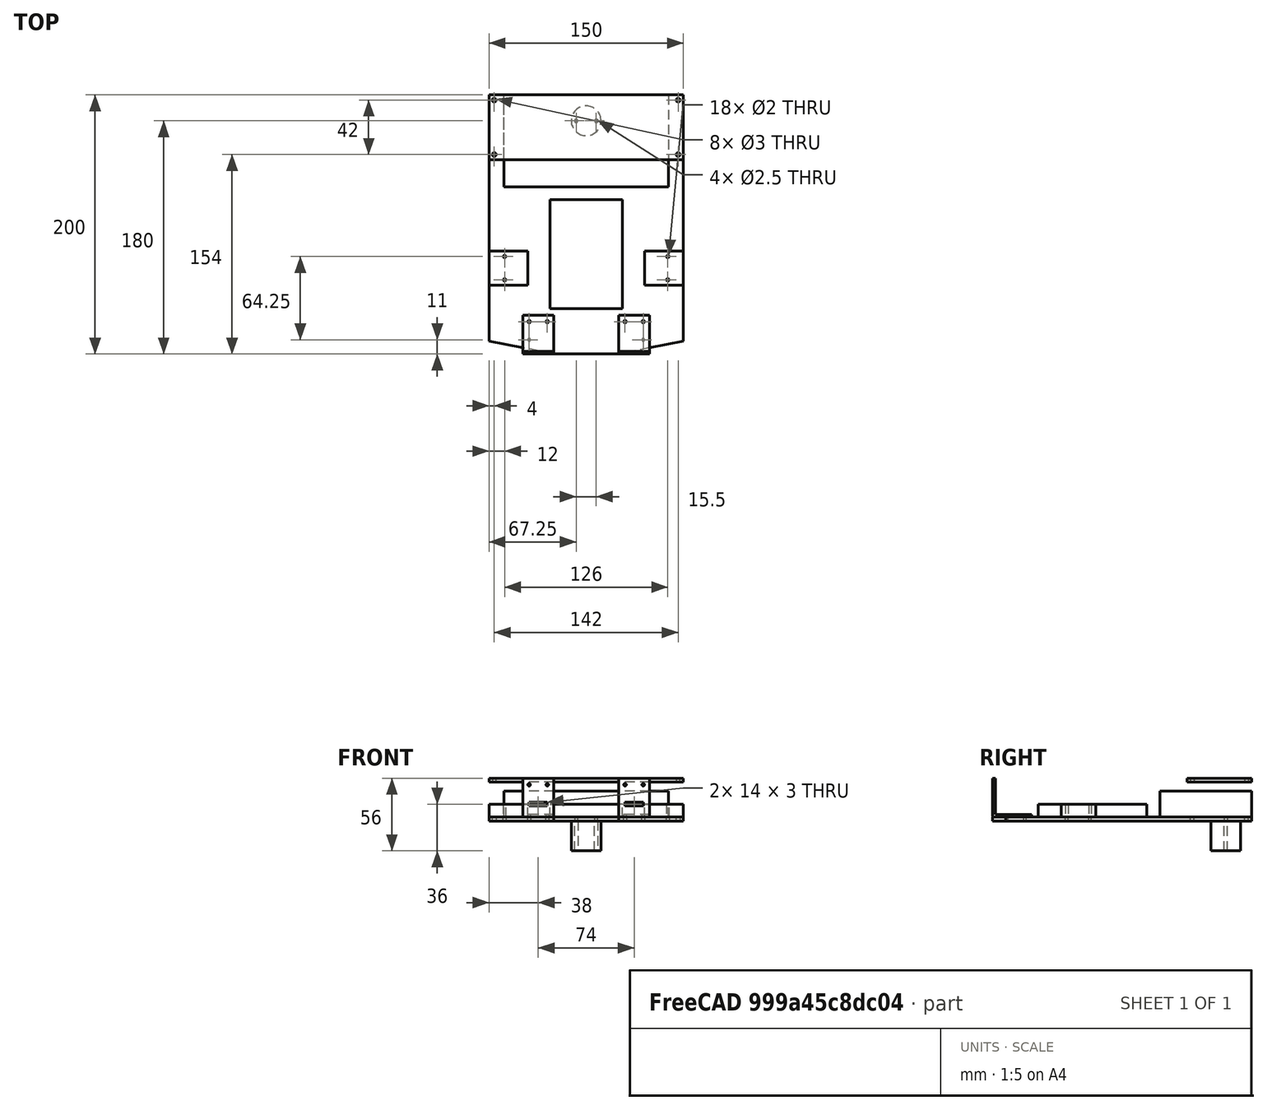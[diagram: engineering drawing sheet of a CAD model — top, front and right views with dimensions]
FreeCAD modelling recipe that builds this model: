
FCSTD DOCUMENT  (FreeCAD 0.21R30769 (Git))
Label: robot
License: All rights reserved
LicenseURL: http://en.wikipedia.org/wiki/All_rights_reserved
objects: TechDraw::DrawViewDimension×57, PartDesign::ShapeBinder×17, PartDesign::Pocket×12, PartDesign::Pad×11, PartDesign::Body×10, TechDraw::DrawProjGroupItem×10, Sketcher::SketchObject×8, TechDraw::DrawSVGTemplate×7, TechDraw::DrawProjGroup×7, TechDraw::DrawPage×7, PartDesign::SubShapeBinder×6, TechDraw::DrawViewAnnotation×3, PartDesign::Fillet×2, App::Part×1
note: 91 computed .brp shape members not serialized (recipe doc carries the construction recipe); baked Part::Feature solids carry a one-line shape summary decoded from their .brp

FEATURE [Sketcher::SketchObject] Sketch  label="ChassisOutline"
  FullyConstrained = true
  MapMode = 5
  Support = -> [XY_Plane]
  sketch-geometry (4):
    g0: LineSegment StartX=-75 StartY=100 StartZ=0 EndX=75 EndY=100 EndZ=0
    g1: LineSegment StartX=75 StartY=100 StartZ=0 EndX=75 EndY=-100 EndZ=0
    g2: LineSegment StartX=75 StartY=-100 StartZ=0 EndX=-75 EndY=-100 EndZ=0
    g3: LineSegment StartX=-75 StartY=-100 StartZ=0 EndX=-75 EndY=100 EndZ=0
  constraints (11):
    c: Coincident(g0,g1)
    c: Coincident(g3,g0)
    c: Horizontal(g0)
    c: Vertical(g1)
    c: Vertical(g3)
    c: Distance(g0) = 150
    c: DistanceY(g2,g0) = 200
    c: Coincident(g2,g1)
    c: Coincident(g2,g3)
    c: Symmetric(g1,g0,g-1)
    c: Horizontal(g2)
FEATURE [Sketcher::SketchObject] Sketch001  label="UpperParts"
  AttachmentOffset = pos=(0,0,3) rot=(0,0,1;0rad)
  ExternalGeometry = -> [Sketch]
  FullyConstrained = true
  MapMode = 5
  Placement = pos=(0,0,3) rot=(0,0,1;0rad)
  Support = -> [XY_Plane]
  sketch-geometry (21):
    g0: LineSegment StartX=-63.5 StartY=100 StartZ=0 EndX=63.5 EndY=100 EndZ=0
    g1: LineSegment StartX=63.5 StartY=100 StartZ=0 EndX=63.5 EndY=29 EndZ=0
    g2: LineSegment StartX=63.5 StartY=29 StartZ=0 EndX=-63.5 EndY=29 EndZ=0
    g3: LineSegment StartX=-63.5 StartY=29 StartZ=0 EndX=-63.5 EndY=100 EndZ=0
    g4: LineSegment StartX=-28 StartY=19 StartZ=0 EndX=28 EndY=19 EndZ=0
    g5: LineSegment StartX=28 StartY=19 StartZ=0 EndX=28 EndY=-65 EndZ=0
    g6: LineSegment StartX=28 StartY=-65 StartZ=0 EndX=-28 EndY=-65 EndZ=0
    g7: LineSegment StartX=-28 StartY=-65 StartZ=0 EndX=-28 EndY=19 EndZ=0
    g8: LineSegment StartX=-75 StartY=-47 StartZ=0 EndX=-45 EndY=-47 EndZ=0
    g9: LineSegment StartX=-45 StartY=-47 StartZ=0 EndX=-45 EndY=-20.5 EndZ=0
    g10: LineSegment StartX=-45 StartY=-20.5 StartZ=0 EndX=-75 EndY=-20.5 EndZ=0
    g11: LineSegment StartX=-75 StartY=-20.5 StartZ=0 EndX=-75 EndY=-47 EndZ=0
    g12: LineSegment StartX=75 StartY=-20.5 StartZ=0 EndX=45 EndY=-20.5 EndZ=0
    g13: LineSegment StartX=45 StartY=-20.5 StartZ=0 EndX=45 EndY=-47 EndZ=0
    g14: LineSegment StartX=45 StartY=-47 StartZ=0 EndX=75 EndY=-47 EndZ=0
    g15: LineSegment StartX=75 StartY=-47 StartZ=0 EndX=75 EndY=-20.5 EndZ=0
    g16: Circle CenterX=-63 CenterY=-24.75 CenterZ=0 NormalX=0 NormalY=0 NormalZ=1 AngleXU=0 Radius=1
    g17: Circle CenterX=-63 CenterY=-42.75 CenterZ=0 NormalX=0 NormalY=0 NormalZ=1 AngleXU=0 Radius=1
    g18: Circle CenterX=63 CenterY=-24.75 CenterZ=0 NormalX=0 NormalY=0 NormalZ=1 AngleXU=0 Radius=1
    g19: Circle CenterX=63 CenterY=-42.75 CenterZ=0 NormalX=0 NormalY=0 NormalZ=1 AngleXU=0 Radius=1
    g20: LineSegment StartX=-45 StartY=-33.75 StartZ=0 EndX=-75 EndY=-33.75 EndZ=0
  constraints (57):
    c: Coincident(g0,g1)
    c: Coincident(g1,g2)
    c: Coincident(g2,g3)
    c: Coincident(g3,g0)
    c: Horizontal(g0)
    c: Vertical(g1)
    c: Vertical(g3)
    c: PointOnObject(g0,g-3)
    c: Coincident(g4,g5)
    c: Coincident(g5,g6)
    c: Coincident(g6,g7)
    c: Coincident(g7,g4)
    c: Horizontal(g6)
    c: Vertical(g5)
    c: Vertical(g7)
    c: Distance(g3) = 71
    c: Distance(g2) = 127
    c: Distance(g6) = 56
    c: Distance(g5) = 84
    c: DistanceY(g4,g2) = 10
    c: Symmetric(g2,g1,g-2)
    c: Symmetric(g4,g4,g-2)
    c: Coincident(g8,g9)
    c: Coincident(g9,g10)
    c: Coincident(g10,g11)
    c: Coincident(g11,g8)
    c: Horizontal(g8)
    c: Horizontal(g10)
    c: Vertical(g9)
    c: Vertical(g11)
    c: PointOnObject(g8,g-4)
    c: Coincident(g12,g13)
    c: Coincident(g13,g14)
    c: Coincident(g14,g15)
    c: Coincident(g15,g12)
    c: Horizontal(g12)
    c: Horizontal(g14)
    c: Vertical(g13)
    c: Vertical(g15)
    c: PointOnObject(g12,g-5)
    c: Equal(g13,g9)
    c: Symmetric(g9,g12,g-2)
    c: DistanceX(g10,g10) = 30
    c: DistanceY(g11,g11) = 26.5
    c: PointOnObject(g20,g9)
    c: PointOnObject(g20,g11)
    c: Symmetric(g10,g8,g20)
    c: Symmetric(g16,g17,g20)
    c: Symmetric(g16,g18,g-2)
    c: Equal(g18,g19)
    c: Equal(g19,g17)
    c: Equal(g17,g16)
    c: Diameter(g16) = 2
    c: DistanceX(g20,g16) = 12
    c: Symmetric(g19,g17,g-2)
    c: DistanceY(g17,g16) = 18
    c: DistanceY(g6,g8) = 18
FEATURE [Sketcher::SketchObject] Sketch002  label="LowerParts"
  ExternalGeometry = -> [Sketch]
  FullyConstrained = true
  MapMode = 5
  Support = -> [XY_Plane]
  sketch-geometry (3):
    g0: Circle CenterX=0 CenterY=80 CenterZ=0 NormalX=0 NormalY=0 NormalZ=1 AngleXU=0 Radius=11.5
    g1: Circle CenterX=-7.75 CenterY=80 CenterZ=0 NormalX=0 NormalY=0 NormalZ=1 AngleXU=0 Radius=1.25
    g2: Circle CenterX=7.75 CenterY=80 CenterZ=0 NormalX=0 NormalY=0 NormalZ=1 AngleXU=0 Radius=1.25
  constraints (8):
    c: PointOnObject(g0,g-2)
    c: Symmetric(g1,g2,g-2)
    c: Horizontal(g0,g1)
    c: Diameter(g2) = 2.5
    c: Equal(g2,g1)
    c: Diameter(g0) = 23
    c: DistanceX(g1,g2) = 15.5
    c: DistanceY(g0,g-3) = 20
FEATURE [PartDesign::ShapeBinder] ShapeBinder
  Support = -> [Sketch,Sketch002,Sketch001]
  TraceSupport = false
FEATURE [PartDesign::Pad] Pad
  Direction = (0,0,1)
  Length = 3
  Length2 = 10
  Profile = -> ShapeBinder
  Type = 0
FEATURE [PartDesign::ShapeBinder] ShapeBinder001
  Support = -> [Sketch001]
  TraceSupport = false
FEATURE [PartDesign::Pocket] Pocket
  BaseFeature = -> Pad
  Direction = (0,0,-1)
  Length = 5
  Length2 = 5
  Profile = -> ShapeBinder001
  Type = 1
FEATURE [PartDesign::ShapeBinder] ShapeBinder002
  Support = -> [Sketch001]
  TraceSupport = false
FEATURE [PartDesign::Pad] Pad001
  Direction = (0,0,1)
  Length = 20
  Length2 = 10
  Profile = -> ShapeBinder002
  Type = 0
FEATURE [PartDesign::Body] Body002  label="BatteryBox"
  Group = -> [ShapeBinder002,Pad001]
  Origin = -> Origin002
  Tip = -> Pad001
FEATURE [PartDesign::ShapeBinder] ShapeBinder003
  Support = -> [Sketch001]
  TraceSupport = false
FEATURE [PartDesign::Pad] Pad002
  Direction = (0,0,1)
  Length = 10
  Length2 = 10
  Profile = -> ShapeBinder003
  Type = 0
FEATURE [PartDesign::Body] Body003  label="Breadboard"
  Group = -> [ShapeBinder003,Pad002]
  Origin = -> Origin003
  Tip = -> Pad002
FEATURE [PartDesign::ShapeBinder] ShapeBinder004
  Support = -> [Sketch001]
  TraceSupport = false
FEATURE [PartDesign::Pad] Pad003
  Direction = (0,0,1)
  Length = 10
  Length2 = 10
  Profile = -> ShapeBinder004
  Type = 0
FEATURE [PartDesign::Body] Body004  label="LeftMotor"
  Group = -> [ShapeBinder004,Pad003]
  Origin = -> Origin004
  Tip = -> Pad003
FEATURE [PartDesign::ShapeBinder] ShapeBinder005
  Support = -> [Sketch001]
  TraceSupport = false
FEATURE [PartDesign::Pad] Pad004
  Direction = (0,0,1)
  Length = 10
  Length2 = 10
  Profile = -> ShapeBinder005
  Type = 0
FEATURE [PartDesign::Body] Body005  label="RightMotor"
  Group = -> [ShapeBinder005,Pad004]
  Origin = -> Origin005
  Tip = -> Pad004
FEATURE [PartDesign::ShapeBinder] ShapeBinder006
  Support = -> [Sketch001]
  TraceSupport = false
FEATURE [PartDesign::Pocket] Pocket001
  BaseFeature = -> Pocket
  Direction = (0,0,-1)
  Length = 5
  Length2 = 5
  Profile = -> ShapeBinder006
  Type = 1
FEATURE [PartDesign::ShapeBinder] ShapeBinder007
  Support = -> [Sketch002]
  TraceSupport = false
FEATURE [PartDesign::Pocket] Pocket002
  BaseFeature = -> Pocket001
  Direction = (0,0,-1)
  Length = 5
  Length2 = 5
  Profile = -> ShapeBinder007
  Reversed = true
  Type = 1
FEATURE [PartDesign::ShapeBinder] ShapeBinder008
  Support = -> [Sketch002]
  TraceSupport = false
FEATURE [PartDesign::Pad] Pad005
  Direction = (0,0,1)
  Length = 23
  Length2 = 10
  Profile = -> ShapeBinder008
  Reversed = true
  Type = 0
FEATURE [PartDesign::Body] Body006  label="Castor"
  Group = -> [ShapeBinder008,Pad005]
  Origin = -> Origin006
  Tip = -> Pad005
FEATURE [TechDraw::DrawSVGTemplate] Template
  Height = 297
  Orientation = 0
  Width = 210
FEATURE [Sketcher::SketchObject] Sketch003  label="BevelFront"
  ExternalGeometry = -> [Sketch]
  FullyConstrained = true
  MapMode = 5
  Support = -> [XY_Plane]
  sketch-geometry (6):
    g0: LineSegment StartX=-75 StartY=-90 StartZ=0 EndX=-25 EndY=-100 EndZ=0
    g1: LineSegment StartX=25 StartY=-100 StartZ=0 EndX=75 EndY=-90 EndZ=0
    g2: LineSegment StartX=-75 StartY=-90 StartZ=0 EndX=-75 EndY=-100 EndZ=0
    g3: LineSegment StartX=-25 StartY=-100 StartZ=0 EndX=-75 EndY=-100 EndZ=0
    g4: LineSegment StartX=25 StartY=-100 StartZ=0 EndX=75 EndY=-100 EndZ=0
    g5: LineSegment StartX=75 StartY=-100 StartZ=0 EndX=75 EndY=-90 EndZ=0
  constraints (14):
    c: PointOnObject(g0,g-4)
    c: PointOnObject(g0,g-3)
    c: Symmetric(g1,g0,g-2)
    c: Symmetric(g0,g1,g-2)
    c: DistanceY(g-4,g0) = 10
    c: DistanceX(g0,g1) = 50
    c: Coincident(g2,g0)
    c: Coincident(g2,g-4)
    c: Coincident(g3,g2)
    c: Coincident(g3,g0)
    c: Coincident(g1,g4)
    c: Coincident(g4,g-5)
    c: Coincident(g4,g5)
    c: Coincident(g5,g1)
FEATURE [PartDesign::ShapeBinder] ShapeBinder009
  Support = -> [Sketch003]
  TraceSupport = false
FEATURE [PartDesign::Pocket] Pocket003
  BaseFeature = -> Pocket002
  Direction = (0,0,-1)
  Length = 5
  Length2 = 5
  Profile = -> ShapeBinder009
  Reversed = true
  Type = 1
FEATURE [PartDesign::ShapeBinder] ShapeBinder010
  Support = -> [Sketch003]
  TraceSupport = false
FEATURE [PartDesign::Pocket] Pocket004
  BaseFeature = -> Pocket003
  Direction = (0,0,-1)
  Length = 5
  Length2 = 5
  Profile = -> ShapeBinder010
  Reversed = true
  Type = 1
FEATURE [TechDraw::DrawSVGTemplate] Template001
  Height = 297
  Orientation = 0
  Width = 210
FEATURE [TechDraw::DrawProjGroupItem] ProjItem001  label="Front001"
  CoarseView = false
  Direction = (0,0,1)
  Focus = 100
  HardHidden = false
  IsoCount = 0
  IsoHidden = false
  IsoVisible = false
  LockPosition = true
  Perspective = false
  Rotation = 0
  RotationVector = (-1,0,0)
  ScaleType = 2
  SeamHidden = false
  SeamVisible = true
  SmoothHidden = false
  SmoothVisible = true
  Source = -> [Pocket002]
  Type = 0
  X = 0
  XDirection = (-1,0,0)
  Y = 0
FEATURE [TechDraw::DrawProjGroup] ProjGroup001
  Anchor = -> ProjItem001
  AutoDistribute = true
  LockPosition = false
  ProjectionType = 0
  Rotation = 0
  ScaleType = 0
  Source = -> [Pocket002]
  Views = -> [ProjItem001]
  X = 105
  Y = 148.5
  spacingX = 15
  spacingY = 15
FEATURE [TechDraw::DrawViewDimension] Dimension012
  AngleOverride = false
  Arbitrary = false
  ArbitraryTolerances = false
  EqualTolerance = true
  ExtensionAngle = 0
  FormatSpec = ⌀%.2f
  FormatSpecOverTolerance = %+.2f
  FormatSpecUnderTolerance = %+.2f
  Inverted = false
  LineAngle = 0
  LockPosition = false
  MeasureType = 1
  OverTolerance = 0
  References2D = -> [ProjItem001]
  Rotation = 0
  ScaleType = 0
  TheoreticalExact = false
  Type = 5
  UnderTolerance = 0
  X = 45.3924
  Y = 74.404
FEATURE [TechDraw::DrawViewDimension] Dimension013
  AngleOverride = false
  Arbitrary = false
  ArbitraryTolerances = false
  EqualTolerance = true
  ExtensionAngle = 0
  FormatSpec = ⌀%.2f
  FormatSpecOverTolerance = %+.2f
  FormatSpecUnderTolerance = %+.2f
  Inverted = false
  LineAngle = 0
  LockPosition = false
  MeasureType = 1
  OverTolerance = 0
  References2D = -> [ProjItem001]
  Rotation = 0
  ScaleType = 0
  TheoreticalExact = false
  Type = 5
  UnderTolerance = 0
  X = 22.3571
  Y = -61.4242
FEATURE [TechDraw::DrawPage] Page001  label="ChassisWithoutBevelsAllDimensions"
  KeepUpdated = true
  NextBalloonIndex = 1
  ProjectionType = 0
  Template = -> Template001
  Views = -> [ProjGroup001,Dimension012,Dimension013]
FEATURE [TechDraw::DrawSVGTemplate] Template002
  Height = 297
  Orientation = 0
  Width = 210
FEATURE [Sketcher::SketchObject] Sketch004  label="DaughterCardOutline"
  AttachmentOffset = pos=(0,0,30) rot=(0,0,1;0rad)
  ExternalGeometry = -> [Sketch]
  FullyConstrained = true
  MapMode = 5
  Placement = pos=(0,0,30) rot=(0,0,1;0rad)
  Support = -> [XY_Plane]
  sketch-geometry (8):
    g0: LineSegment StartX=-75 StartY=100 StartZ=0 EndX=75 EndY=100 EndZ=0
    g1: LineSegment StartX=75 StartY=100 StartZ=0 EndX=75 EndY=50 EndZ=0
    g2: LineSegment StartX=75 StartY=50 StartZ=0 EndX=-75 EndY=50 EndZ=0
    g3: LineSegment StartX=-75 StartY=50 StartZ=0 EndX=-75 EndY=100 EndZ=0
    g4: Circle CenterX=-71 CenterY=96 CenterZ=0 NormalX=0 NormalY=0 NormalZ=1 AngleXU=0 Radius=1.5
    g5: Circle CenterX=-71 CenterY=54 CenterZ=0 NormalX=0 NormalY=0 NormalZ=1 AngleXU=0 Radius=1.5
    g6: Circle CenterX=71 CenterY=96 CenterZ=0 NormalX=0 NormalY=0 NormalZ=1 AngleXU=0 Radius=1.5
    g7: Circle CenterX=71 CenterY=54 CenterZ=0 NormalX=0 NormalY=0 NormalZ=1 AngleXU=0 Radius=1.5
  constraints (22):
    c: Coincident(g0,g1)
    c: Coincident(g1,g2)
    c: Coincident(g2,g3)
    c: Coincident(g3,g0)
    c: Horizontal(g0)
    c: Horizontal(g2)
    c: Vertical(g1)
    c: Vertical(g3)
    c: Coincident(g0,g-4)
    c: PointOnObject(g1,g-5)
    c: DistanceY(g3,g3) = 50
    c: DistanceY(g4,g0) = 4
    c: DistanceX(g0,g4) = 4
    c: Vertical(g5,g4)
    c: Horizontal(g5,g7)
    c: Equal(g6,g4)
    c: Equal(g4,g5)
    c: Equal(g5,g7)
    c: Diameter(g6) = 3
    c: Vertical(g6,g7)
    c: Symmetric(g4,g6,g-2)
    c: DistanceY(g2,g5) = 4
FEATURE [PartDesign::ShapeBinder] ShapeBinder011
  Support = -> [Sketch004]
  TraceSupport = false
FEATURE [PartDesign::Pocket] Pocket005
  BaseFeature = -> Pocket004
  Direction = (0,0,-1)
  Length = 5
  Length2 = 5
  Profile = -> ShapeBinder011
  Reversed = true
  Type = 1
FEATURE [PartDesign::ShapeBinder] ShapeBinder012
  Support = -> [Sketch004]
  TraceSupport = false
FEATURE [PartDesign::Pad] Pad006
  Direction = (0,0,1)
  Length = 3
  Length2 = 10
  Profile = -> ShapeBinder012
  Type = 0
FEATURE [PartDesign::Body] Body007  label="DaughterCard"
  Group = -> [ShapeBinder012,Pad006]
  Origin = -> Origin007
  Tip = -> Pad006
FEATURE [TechDraw::DrawSVGTemplate] Template003
  Height = 297
  Orientation = 0
  Width = 210
FEATURE [TechDraw::DrawProjGroupItem] ProjItem003  label="Front003"
  CoarseView = false
  Direction = (0,0,1)
  Focus = 100
  HardHidden = false
  IsoCount = 0
  IsoHidden = false
  IsoVisible = false
  LockPosition = true
  Perspective = false
  Rotation = 0
  RotationVector = (1,0,0)
  ScaleType = 2
  SeamHidden = false
  SeamVisible = true
  SmoothHidden = false
  SmoothVisible = true
  Source = -> [Body007]
  Type = 0
  X = 0
  XDirection = (1,0,0)
  Y = 0
FEATURE [TechDraw::DrawProjGroup] ProjGroup003
  Anchor = -> ProjItem003
  AutoDistribute = true
  LockPosition = false
  ProjectionType = 0
  Rotation = 0
  ScaleType = 0
  Source = -> [Body007]
  Views = -> [ProjItem003]
  X = 104.394
  Y = 152.44
  spacingX = 15
  spacingY = 15
FEATURE [TechDraw::DrawViewDimension] Dimension028
  AngleOverride = false
  Arbitrary = false
  ArbitraryTolerances = false
  EqualTolerance = true
  ExtensionAngle = 0
  FormatSpec = %.2f
  FormatSpecOverTolerance = %+.2f
  FormatSpecUnderTolerance = %+.2f
  Inverted = false
  LineAngle = 0
  LockPosition = false
  MeasureType = 1
  OverTolerance = 0
  References2D = -> [ProjItem003]
  Rotation = 0
  ScaleType = 0
  TheoreticalExact = false
  Type = 1
  UnderTolerance = 0
  X = 0
  Y = 39.9255
FEATURE [TechDraw::DrawViewDimension] Dimension029
  AngleOverride = false
  Arbitrary = false
  ArbitraryTolerances = false
  EqualTolerance = true
  ExtensionAngle = 0
  FormatSpec = %.2f
  FormatSpecOverTolerance = %+.2f
  FormatSpecUnderTolerance = %+.2f
  Inverted = false
  LineAngle = 0
  LockPosition = false
  MeasureType = 1
  OverTolerance = 0
  References2D = -> [ProjItem003]
  Rotation = 0
  ScaleType = 0
  TheoreticalExact = false
  Type = 1
  UnderTolerance = 0
  X = -62.1643
  Y = 16.3949
FEATURE [TechDraw::DrawViewDimension] Dimension030
  AngleOverride = false
  Arbitrary = false
  ArbitraryTolerances = false
  EqualTolerance = true
  ExtensionAngle = 0
  FormatSpec = %.2f
  FormatSpecOverTolerance = %+.2f
  FormatSpecUnderTolerance = %+.2f
  Inverted = false
  LineAngle = 0
  LockPosition = false
  MeasureType = 1
  OverTolerance = 0
  References2D = -> [ProjItem003]
  Rotation = 0
  ScaleType = 0
  TheoreticalExact = false
  Type = 2
  UnderTolerance = 0
  X = -50.209
  Y = 15.356
FEATURE [TechDraw::DrawViewDimension] Dimension031
  AngleOverride = false
  Arbitrary = false
  ArbitraryTolerances = false
  EqualTolerance = true
  ExtensionAngle = 0
  FormatSpec = %.2f
  FormatSpecOverTolerance = %+.2f
  FormatSpecUnderTolerance = %+.2f
  Inverted = false
  LineAngle = 0
  LockPosition = false
  MeasureType = 1
  OverTolerance = 0
  References2D = -> [ProjItem003]
  Rotation = 0
  ScaleType = 0
  TheoreticalExact = false
  Type = 2
  UnderTolerance = 0
  X = -83.5302
  Y = 3.19164
FEATURE [TechDraw::DrawViewDimension] Dimension032
  AngleOverride = false
  Arbitrary = false
  ArbitraryTolerances = false
  EqualTolerance = true
  ExtensionAngle = 0
  FormatSpec = ⌀%.2f
  FormatSpecOverTolerance = %+.2f
  FormatSpecUnderTolerance = %+.2f
  Inverted = false
  LineAngle = 0
  LockPosition = false
  MeasureType = 1
  OverTolerance = 0
  References2D = -> [ProjItem003]
  Rotation = 0
  ScaleType = 0
  TheoreticalExact = false
  Type = 5
  UnderTolerance = 0
  X = -57.1755
  Y = -10.3746
FEATURE [TechDraw::DrawPage] Page003  label="DaughterCardDimensions"
  KeepUpdated = true
  NextBalloonIndex = 1
  ProjectionType = 0
  Template = -> Template003
  Views = -> [ProjGroup003,Dimension028,Dimension029,Dimension030,Dimension031,Dimension032]
FEATURE [App::Part] Part
  Origin = -> Origin008
FEATURE [Sketcher::SketchObject] Sketch005  label="SensorBracketBase"
  AttachmentOffset = pos=(0,0,3) rot=(0,0,1;0rad)
  ExternalGeometry = -> [Sketch]
  FullyConstrained = true
  MapMode = 5
  Placement = pos=(0,0,3) rot=(0,0,1;0rad)
  Support = -> [XY_Plane]
  sketch-geometry (13):
    g0: LineSegment StartX=-49 StartY=-100 StartZ=0 EndX=-25 EndY=-100 EndZ=0
    g1: LineSegment StartX=-25 StartY=-100 StartZ=0 EndX=-25 EndY=-70 EndZ=0
    g2: LineSegment StartX=-25 StartY=-70 StartZ=0 EndX=-49 EndY=-70 EndZ=0
    g3: LineSegment StartX=-49 StartY=-70 StartZ=0 EndX=-49 EndY=-100 EndZ=0
    g4: LineSegment StartX=25 StartY=-100 StartZ=0 EndX=49 EndY=-100 EndZ=0
    g5: LineSegment StartX=49 StartY=-100 StartZ=0 EndX=49 EndY=-70 EndZ=0
    g6: LineSegment StartX=49 StartY=-70 StartZ=0 EndX=25 EndY=-70 EndZ=0
    g7: LineSegment StartX=25 StartY=-70 StartZ=0 EndX=25 EndY=-100 EndZ=0
    g8: Circle CenterX=-30 CenterY=-75 CenterZ=0 NormalX=0 NormalY=0 NormalZ=1 AngleXU=0 Radius=1
    g9: Circle CenterX=-44 CenterY=-75 CenterZ=0 NormalX=0 NormalY=0 NormalZ=1 AngleXU=0 Radius=1
    g10: Circle CenterX=30 CenterY=-75 CenterZ=0 NormalX=0 NormalY=0 NormalZ=1 AngleXU=0 Radius=1
    g11: Circle CenterX=44 CenterY=-75 CenterZ=0 NormalX=0 NormalY=0 NormalZ=1 AngleXU=0 Radius=1
    g12: LineSegment StartX=-37 StartY=-70 StartZ=0 EndX=-37 EndY=-100 EndZ=0
  constraints (35):
    c: Coincident(g0,g1)
    c: Coincident(g1,g2)
    c: Coincident(g2,g3)
    c: Coincident(g3,g0)
    c: Horizontal(g0)
    c: Horizontal(g2)
    c: Vertical(g1)
    c: Vertical(g3)
    c: PointOnObject(g0,g-3)
    c: Coincident(g4,g5)
    c: Coincident(g5,g6)
    c: Coincident(g6,g7)
    c: Coincident(g7,g4)
    c: Horizontal(g4)
    c: Horizontal(g6)
    c: Vertical(g5)
    c: Vertical(g7)
    c: PointOnObject(g4,g-3)
    c: DistanceY(g1,g1) = 30
    c: Equal(g2,g6)
    c: Symmetric(g1,g6,g-2)
    c: DistanceX(g2,g2) = 24
    c: DistanceX(g0,g4) = 50
    c: PointOnObject(g12,g2)
    c: PointOnObject(g12,g0)
    c: Symmetric(g2,g1,g12)
    c: Symmetric(g9,g8,g12)
    c: Symmetric(g8,g10,g-2)
    c: Symmetric(g11,g9,g-2)
    c: Equal(g9,g8)
    c: Equal(g8,g10)
    c: Equal(g10,g11)
    c: Diameter(g9) = 2
    c: DistanceX(g9,g8) = 14
    c: DistanceY(g9,g2) = 5
FEATURE [PartDesign::ShapeBinder] ShapeBinder013
  Support = -> [Sketch005]
  TraceSupport = false
FEATURE [PartDesign::Pad] Pad007
  Direction = (0,0,1)
  Length = 2
  Length2 = 10
  Profile = -> ShapeBinder013
  Type = 0
FEATURE [PartDesign::ShapeBinder] ShapeBinder014
  Support = -> [Sketch005]
  TraceSupport = false
FEATURE [PartDesign::Pad] Pad008
  Direction = (0,0,1)
  Length = 2
  Length2 = 10
  Profile = -> ShapeBinder014
  Type = 0
FEATURE [Sketcher::SketchObject] Sketch007  label="SensorBracketFront"
  AttachmentOffset = pos=(0,0,100) rot=(0,0,1;0rad)
  ExternalGeometry = -> [Sketch005]
  FullyConstrained = true
  MapMode = 5
  Placement = pos=(0,-100,-2.22e-14) rot=(1,0,0;1.5708rad)
  Support = -> [XZ_Plane]
  sketch-geometry (21):
    g0: LineSegment StartX=-49 StartY=3 StartZ=0 EndX=-25 EndY=3 EndZ=0
    g1: LineSegment StartX=-25 StartY=3 StartZ=0 EndX=-25 EndY=33 EndZ=0
    g2: LineSegment StartX=-25 StartY=33 StartZ=0 EndX=-49 EndY=33 EndZ=0
    g3: LineSegment StartX=-49 StartY=33 StartZ=0 EndX=-49 EndY=3 EndZ=0
    g4: LineSegment StartX=-37 StartY=33 StartZ=0 EndX=-37 EndY=3 EndZ=0
    g5: Circle CenterX=-44 CenterY=28 CenterZ=0 NormalX=0 NormalY=0 NormalZ=1 AngleXU=0 Radius=1
    g6: Circle CenterX=-30 CenterY=28 CenterZ=0 NormalX=0 NormalY=0 NormalZ=1 AngleXU=0 Radius=1
    g7: LineSegment StartX=25 StartY=3 StartZ=0 EndX=49 EndY=3 EndZ=0
    g8: LineSegment StartX=49 StartY=3 StartZ=0 EndX=49 EndY=33 EndZ=0
    g9: LineSegment StartX=49 StartY=33 StartZ=0 EndX=25 EndY=33 EndZ=0
    g10: LineSegment StartX=25 StartY=33 StartZ=0 EndX=25 EndY=3 EndZ=0
    g11: Circle CenterX=30 CenterY=28 CenterZ=0 NormalX=0 NormalY=0 NormalZ=1 AngleXU=0 Radius=1
    g12: Circle CenterX=44 CenterY=28 CenterZ=0 NormalX=0 NormalY=0 NormalZ=1 AngleXU=0 Radius=1
    g13: LineSegment StartX=-44 StartY=11.5 StartZ=0 EndX=-30 EndY=11.5 EndZ=0
    g14: LineSegment StartX=-30 StartY=11.5 StartZ=0 EndX=-30 EndY=14.5 EndZ=0
    g15: LineSegment StartX=-30 StartY=14.5 StartZ=0 EndX=-44 EndY=14.5 EndZ=0
    g16: LineSegment StartX=-44 StartY=14.5 StartZ=0 EndX=-44 EndY=11.5 EndZ=0
    g17: LineSegment StartX=30 StartY=14.5 StartZ=0 EndX=44 EndY=14.5 EndZ=0
    g18: LineSegment StartX=44 StartY=14.5 StartZ=0 EndX=44 EndY=11.5 EndZ=0
    g19: LineSegment StartX=44 StartY=11.5 StartZ=0 EndX=30 EndY=11.5 EndZ=0
    g20: LineSegment StartX=30 StartY=11.5 StartZ=0 EndX=30 EndY=14.5 EndZ=0
  constraints (53):
    c: Coincident(g0,g1)
    c: Coincident(g1,g2)
    c: Coincident(g2,g3)
    c: Coincident(g3,g0)
    c: Horizontal(g2)
    c: Vertical(g1)
    c: Vertical(g3)
    c: Coincident(g0,g-3)
    c: Coincident(g0,g-3)
    c: DistanceY(g3,g3) = 30
    c: PointOnObject(g4,g2)
    c: PointOnObject(g4,g0)
    c: Symmetric(g1,g2,g4)
    c: Coincident(g7,g8)
    c: Coincident(g8,g9)
    c: Coincident(g9,g10)
    c: Coincident(g10,g7)
    c: Horizontal(g9)
    c: Vertical(g8)
    c: Vertical(g10)
    c: Coincident(g7,g-4)
    c: Coincident(g7,g-4)
    c: Equal(g1,g10)
    c: Symmetric(g12,g5,g-2)
    c: Symmetric(g6,g11,g-2)
    c: Equal(g5,g6)
    c: Equal(g6,g11)
    c: Equal(g11,g12)
    c: Symmetric(g6,g5,g4)
    c: Diameter(g5) = 2
    c: DistanceX(g5,g6) = 14
    c: DistanceY(g5,g2) = 5
    c: Coincident(g13,g14)
    c: Coincident(g14,g15)
    c: Coincident(g15,g16)
    c: Coincident(g16,g13)
    c: Horizontal(g15)
    c: Vertical(g14)
    c: Vertical(g16)
    c: Symmetric(g13,g13,g4)
    c: DistanceX(g13,g13) = 14
    c: DistanceY(g13,g6) = 16.5
    c: DistanceY(g14,g14) = 3
    c: Coincident(g17,g18)
    c: Coincident(g18,g19)
    c: Coincident(g19,g20)
    c: Coincident(g20,g17)
    c: Horizontal(g17)
    c: Horizontal(g19)
    c: Vertical(g18)
    c: Vertical(g20)
    c: Symmetric(g17,g14,g-2)
    c: Symmetric(g13,g18,g-2)
FEATURE [PartDesign::ShapeBinder] ShapeBinder015
  Support = -> [Sketch007]
  TraceSupport = false
FEATURE [PartDesign::Pad] Pad009
  BaseFeature = -> Pad007
  Direction = (0,1,4e-16)
  Length = 2
  Length2 = 10
  Profile = -> ShapeBinder015
  Type = 0
FEATURE [PartDesign::SubShapeBinder] Binder
  BindCopyOnChange = 0
  BindMode = 0
  ClaimChildren = false
  Context = -> Body009 [Binder.]
  Fuse = false
  MakeFace = true
  OffsetFill = false
  OffsetIntersection = false
  OffsetJoinType = 0
  OffsetOpenResult = false
  PartialLoad = false
  Relative = true
  Support = -> [Body[Sketch007.Edge11,Sketch007.Edge12,Sketch007.Edge9,Sketch007.Edge10,Sketch007.Edge8,Sketch007.Edge7]]
  _Version = 2
FEATURE [PartDesign::Pad] Pad010
  BaseFeature = -> Pad008
  Direction = (0,1,4e-16)
  Length = 2
  Length2 = 10
  Profile = -> Binder
  Type = 0
FEATURE [PartDesign::SubShapeBinder] Binder001
  BindCopyOnChange = 0
  BindMode = 0
  ClaimChildren = false
  Context = -> Body008 [Binder001.]
  Fuse = false
  MakeFace = true
  OffsetFill = false
  OffsetIntersection = false
  OffsetJoinType = 0
  OffsetOpenResult = false
  PartialLoad = false
  Relative = true
  Support = -> [Body[Sketch007.Edge15,Sketch007.Edge16,Sketch007.Edge13,Sketch007.Edge14]]
  _Version = 2
FEATURE [PartDesign::Pocket] Pocket006
  BaseFeature = -> Pad009
  Direction = (0,-1,0)
  Length = 5
  Length2 = 5
  Profile = -> Binder001
  Reversed = true
  Type = 1
FEATURE [PartDesign::SubShapeBinder] Binder002
  BindCopyOnChange = 0
  BindMode = 0
  ClaimChildren = false
  Context = -> Body009 [Binder002.]
  Fuse = false
  MakeFace = true
  OffsetFill = false
  OffsetIntersection = false
  OffsetJoinType = 0
  OffsetOpenResult = false
  PartialLoad = false
  Relative = true
  Support = -> [Body[Sketch007.Edge17,Sketch007.Edge20,Sketch007.Edge19,Sketch007.Edge18]]
  _Version = 2
FEATURE [PartDesign::Pocket] Pocket007
  BaseFeature = -> Pad010
  Direction = (0,-1,0)
  Length = 5
  Length2 = 5
  Profile = -> Binder002
  Reversed = true
  Type = 1
FEATURE [PartDesign::SubShapeBinder] Binder003
  BindCopyOnChange = 0
  BindMode = 0
  ClaimChildren = false
  Context = -> Body001 [Binder003.]
  Fuse = false
  MakeFace = true
  OffsetFill = false
  OffsetIntersection = false
  OffsetJoinType = 0
  OffsetOpenResult = false
  PartialLoad = false
  Relative = true
  Support = -> [Body[Sketch005.Edge10,Sketch005.Edge9]]
  _Version = 2
FEATURE [PartDesign::Pocket] Pocket008
  BaseFeature = -> Pocket005
  Direction = (0,0,-1)
  Length = 5
  Length2 = 5
  Profile = -> Binder003
  Type = 1
FEATURE [PartDesign::SubShapeBinder] Binder004
  BindCopyOnChange = 0
  BindMode = 0
  ClaimChildren = false
  Context = -> Body001 [Binder004.]
  Fuse = false
  MakeFace = true
  OffsetFill = false
  OffsetIntersection = false
  OffsetJoinType = 0
  OffsetOpenResult = false
  PartialLoad = false
  Relative = true
  Support = -> [Body[Sketch005.Edge11,Sketch005.Edge12]]
  _Version = 2
FEATURE [PartDesign::Pocket] Pocket009
  BaseFeature = -> Pocket008
  Direction = (0,0,-1)
  Length = 5
  Length2 = 5
  Profile = -> Binder004
  Type = 1
FEATURE [PartDesign::SubShapeBinder] Binder005
  BindCopyOnChange = 0
  BindMode = 0
  ClaimChildren = false
  Context = -> Body001 [Binder005.]
  Fuse = false
  MakeFace = true
  OffsetFill = false
  OffsetIntersection = false
  OffsetJoinType = 0
  OffsetOpenResult = false
  PartialLoad = false
  Relative = true
  Support = -> [Body[Sketch004.Edge5,Sketch004.Edge6,Sketch004.Edge8,Sketch004.Vertex7,Sketch004.Edge7]]
  _Version = 2
FEATURE [PartDesign::Pocket] Pocket010
  BaseFeature = -> Pocket009
  Direction = (0,0,-1)
  Length = 5
  Length2 = 5
  Profile = -> Binder005
  Type = 1
FEATURE [TechDraw::DrawSVGTemplate] Template004
  Height = 297
  Orientation = 0
  Width = 210
FEATURE [PartDesign::Fillet] Fillet
  Base = -> Pocket006 [Edge21]
  BaseFeature = -> Pocket006
  Radius = 1
  SupportTransform = false
  UseAllEdges = false
FEATURE [PartDesign::Body] Body008  label="LeftSensorBracket"
  Group = -> [ShapeBinder013,Pad007,ShapeBinder015,Pad009,Binder001,Pocket006,Fillet]
  Origin = -> Origin009
  Tip = -> Fillet
FEATURE [TechDraw::DrawProjGroupItem] ProjItem004  label="Front004"
  CoarseView = false
  Direction = (0,-1,0)
  Focus = 100
  HardHidden = false
  IsoCount = 0
  IsoHidden = false
  IsoVisible = false
  LockPosition = true
  Perspective = false
  Rotation = 0
  RotationVector = (1,0,0)
  Scale = 1.5
  ScaleType = 2
  SeamHidden = false
  SeamVisible = true
  SmoothHidden = false
  SmoothVisible = true
  Source = -> [Body008]
  Type = 0
  X = 0
  XDirection = (1,0,0)
  Y = 0
FEATURE [TechDraw::DrawProjGroupItem] ProjItem005  label="FrontTopRight"
  CoarseView = false
  Direction = (0.57735,-0.57735,0.57735)
  Focus = 100
  HardHidden = false
  IsoCount = 0
  IsoHidden = false
  IsoVisible = false
  LockPosition = false
  Perspective = false
  Rotation = 0
  RotationVector = (1,0,0)
  Scale = 1.5
  ScaleType = 2
  SeamHidden = false
  SeamVisible = true
  SmoothHidden = false
  SmoothVisible = true
  Source = -> [Body008]
  Type = 7
  X = -61.6378
  XDirection = (0.707107,0.707107,0)
  Y = -63.5981
FEATURE [TechDraw::DrawProjGroupItem] ProjItem006  label="Right"
  CoarseView = false
  Direction = (1,-1e-16,0)
  Focus = 100
  HardHidden = false
  IsoCount = 0
  IsoHidden = false
  IsoVisible = false
  LockPosition = false
  Perspective = false
  Rotation = 0
  RotationVector = (1,0,0)
  Scale = 1.5
  ScaleType = 2
  SeamHidden = false
  SeamVisible = true
  SmoothHidden = false
  SmoothVisible = true
  Source = -> [Body008]
  Type = 2
  X = -61.6378
  XDirection = (1e-16,1,0)
  Y = 0
FEATURE [PartDesign::Fillet] Fillet001
  Base = -> Pocket007 [Edge21]
  BaseFeature = -> Pocket007
  Radius = 1
  SupportTransform = false
  UseAllEdges = false
FEATURE [PartDesign::Body] Body009  label="RightSensorBracket"
  Group = -> [ShapeBinder014,Pad008,Binder,Pad010,Binder002,Pocket007,Fillet001]
  Origin = -> Origin010
  Tip = -> Fillet001
FEATURE [TechDraw::DrawViewDimension] Dimension033
  AngleOverride = false
  Arbitrary = false
  ArbitraryTolerances = false
  EqualTolerance = true
  ExtensionAngle = 0
  FormatSpec = %.2f
  FormatSpecOverTolerance = %+.2f
  FormatSpecUnderTolerance = %+.2f
  Inverted = false
  LineAngle = 0
  LockPosition = false
  MeasureType = 1
  OverTolerance = 0
  References2D = -> [ProjItem004]
  Rotation = 0
  ScaleType = 0
  TheoreticalExact = false
  Type = 1
  UnderTolerance = 0
  X = -2.05098
  Y = 34.5712
FEATURE [TechDraw::DrawViewDimension] Dimension034
  AngleOverride = false
  Arbitrary = false
  ArbitraryTolerances = false
  EqualTolerance = true
  ExtensionAngle = 0
  FormatSpec = %.2f
  FormatSpecOverTolerance = %+.2f
  FormatSpecUnderTolerance = %+.2f
  Inverted = false
  LineAngle = 0
  LockPosition = false
  MeasureType = 1
  OverTolerance = 0
  References2D = -> [ProjItem004]
  Rotation = 0
  ScaleType = 0
  TheoreticalExact = false
  Type = 1
  UnderTolerance = 0
  X = 0
  Y = 0.668294
FEATURE [TechDraw::DrawViewDimension] Dimension035
  AngleOverride = false
  Arbitrary = false
  ArbitraryTolerances = false
  EqualTolerance = true
  ExtensionAngle = 0
  FormatSpec = %.2f
  FormatSpecOverTolerance = %+.2f
  FormatSpecUnderTolerance = %+.2f
  Inverted = false
  LineAngle = 0
  LockPosition = false
  MeasureType = 1
  OverTolerance = 0
  References2D = -> [ProjItem004]
  Rotation = 0
  ScaleType = 0
  TheoreticalExact = false
  Type = 1
  UnderTolerance = 0
  X = 0.341829
  Y = 19.7781
FEATURE [TechDraw::DrawViewDimension] Dimension036
  AngleOverride = false
  Arbitrary = false
  ArbitraryTolerances = false
  EqualTolerance = true
  ExtensionAngle = 0
  FormatSpec = %.2f
  FormatSpecOverTolerance = %+.2f
  FormatSpecUnderTolerance = %+.2f
  Inverted = false
  LineAngle = 0
  LockPosition = false
  MeasureType = 1
  OverTolerance = 0
  References2D = -> [ProjItem004]
  Rotation = 0
  ScaleType = 0
  TheoreticalExact = false
  Type = 2
  UnderTolerance = 0
  X = -22.5787
  Y = 18.8572
FEATURE [TechDraw::DrawViewDimension] Dimension037
  AngleOverride = false
  Arbitrary = false
  ArbitraryTolerances = false
  EqualTolerance = true
  ExtensionAngle = 0
  FormatSpec = %.2f
  FormatSpecOverTolerance = %+.2f
  FormatSpecUnderTolerance = %+.2f
  Inverted = false
  LineAngle = 0
  LockPosition = false
  MeasureType = 1
  OverTolerance = 0
  References2D = -> [ProjItem004]
  Rotation = 0
  ScaleType = 0
  TheoreticalExact = false
  Type = 1
  UnderTolerance = 0
  X = -14.0107
  Y = 8.70284
FEATURE [TechDraw::DrawViewDimension] Dimension038
  AngleOverride = false
  Arbitrary = false
  ArbitraryTolerances = false
  EqualTolerance = true
  ExtensionAngle = 0
  FormatSpec = %.2f
  FormatSpecOverTolerance = %+.2f
  FormatSpecUnderTolerance = %+.2f
  Inverted = false
  LineAngle = 0
  LockPosition = false
  MeasureType = 1
  OverTolerance = 0
  References2D = -> [ProjItem004]
  Rotation = 0
  ScaleType = 0
  TheoreticalExact = false
  Type = 2
  UnderTolerance = 0
  X = 13.4739
  Y = -13.9774
FEATURE [TechDraw::DrawViewDimension] Dimension039
  AngleOverride = false
  Arbitrary = false
  ArbitraryTolerances = false
  EqualTolerance = true
  ExtensionAngle = 0
  FormatSpec = %.2f
  FormatSpecOverTolerance = %+.2f
  FormatSpecUnderTolerance = %+.2f
  Inverted = false
  LineAngle = 0
  LockPosition = false
  MeasureType = 1
  OverTolerance = 0
  References2D = -> [ProjItem004]
  Rotation = 0
  ScaleType = 0
  TheoreticalExact = false
  Type = 2
  UnderTolerance = 0
  X = -29.1725
  Y = 4.39281
FEATURE [TechDraw::DrawProjGroupItem] ProjItem007  label="Top"
  CoarseView = false
  Direction = (0,0,1)
  Focus = 100
  HardHidden = false
  IsoCount = 0
  IsoHidden = false
  IsoVisible = false
  LockPosition = false
  Perspective = false
  Rotation = 0
  RotationVector = (1,0,0)
  Scale = 1.5
  ScaleType = 2
  SeamHidden = false
  SeamVisible = true
  SmoothHidden = false
  SmoothVisible = true
  Source = -> [Body008]
  Type = 4
  X = 0
  XDirection = (1,0,0)
  Y = -63.5981
FEATURE [TechDraw::DrawProjGroup] ProjGroup004
  Anchor = -> ProjItem004
  AutoDistribute = true
  LockPosition = false
  ProjectionType = 0
  Rotation = 0
  Scale = 1.5
  ScaleType = 1
  Source = -> [Body008]
  Views = -> [ProjItem004,ProjItem005,ProjItem006,ProjItem007]
  X = 141.302
  Y = 167.779
  spacingX = 15
  spacingY = 15
FEATURE [TechDraw::DrawViewDimension] Dimension040
  AngleOverride = false
  Arbitrary = false
  ArbitraryTolerances = false
  EqualTolerance = true
  ExtensionAngle = 0
  FormatSpec = %.2f
  FormatSpecOverTolerance = %+.2f
  FormatSpecUnderTolerance = %+.2f
  Inverted = false
  LineAngle = 0
  LockPosition = false
  MeasureType = 1
  OverTolerance = 0
  References2D = -> [ProjItem007]
  Rotation = 0
  ScaleType = 0
  TheoreticalExact = false
  Type = 1
  UnderTolerance = 0
  X = -1.70915
  Y = 1.01572
FEATURE [TechDraw::DrawViewDimension] Dimension041
  AngleOverride = false
  Arbitrary = false
  ArbitraryTolerances = false
  EqualTolerance = true
  ExtensionAngle = 0
  FormatSpec = %.2f
  FormatSpecOverTolerance = %+.2f
  FormatSpecUnderTolerance = %+.2f
  Inverted = false
  LineAngle = 0
  LockPosition = false
  MeasureType = 1
  OverTolerance = 0
  References2D = -> [ProjItem007]
  Rotation = 0
  ScaleType = 0
  TheoreticalExact = false
  Type = 2
  UnderTolerance = 0
  X = -22.8951
  Y = 18.5281
FEATURE [TechDraw::DrawViewDimension] Dimension042
  AngleOverride = false
  Arbitrary = false
  ArbitraryTolerances = false
  EqualTolerance = true
  ExtensionAngle = 0
  FormatSpec = %.2f
  FormatSpecOverTolerance = %+.2f
  FormatSpecUnderTolerance = %+.2f
  Inverted = false
  LineAngle = 0
  LockPosition = false
  MeasureType = 1
  OverTolerance = 0
  References2D = -> [ProjItem007]
  Rotation = 0
  ScaleType = 0
  TheoreticalExact = false
  Type = 1
  UnderTolerance = 0
  X = -14.5918
  Y = 35.0277
FEATURE [TechDraw::DrawViewDimension] Dimension043
  AngleOverride = false
  Arbitrary = false
  ArbitraryTolerances = false
  EqualTolerance = true
  ExtensionAngle = 0
  FormatSpec = ⌀%.2f
  FormatSpecOverTolerance = %+.2f
  FormatSpecUnderTolerance = %+.2f
  Inverted = false
  LineAngle = 0
  LockPosition = false
  MeasureType = 1
  OverTolerance = 0
  References2D = -> [ProjItem004]
  Rotation = 0
  ScaleType = 0
  TheoreticalExact = false
  Type = 5
  UnderTolerance = 0
  X = 28.5428
  Y = 24.4408
FEATURE [TechDraw::DrawViewDimension] Dimension044
  AngleOverride = false
  Arbitrary = false
  ArbitraryTolerances = false
  EqualTolerance = true
  ExtensionAngle = 0
  FormatSpec = ⌀%.2f
  FormatSpecOverTolerance = %+.2f
  FormatSpecUnderTolerance = %+.2f
  Inverted = false
  LineAngle = 0
  LockPosition = false
  MeasureType = 1
  OverTolerance = 0
  References2D = -> [ProjItem007]
  Rotation = 0
  ScaleType = 0
  TheoreticalExact = false
  Type = 5
  UnderTolerance = 0
  X = 31.961
  Y = 34.1829
FEATURE [TechDraw::DrawViewDimension] Dimension045
  AngleOverride = false
  Arbitrary = false
  ArbitraryTolerances = false
  EqualTolerance = true
  ExtensionAngle = 0
  FormatSpec = %.2f
  FormatSpecOverTolerance = %+.2f
  FormatSpecUnderTolerance = %+.2f
  Inverted = false
  LineAngle = 0
  LockPosition = false
  MeasureType = 1
  OverTolerance = 0
  References2D = -> [ProjItem007]
  Rotation = 0
  ScaleType = 0
  TheoreticalExact = false
  Type = 2
  UnderTolerance = 0
  X = -30.8186
  Y = 3.1964
FEATURE [TechDraw::DrawViewDimension] Dimension046
  AngleOverride = false
  Arbitrary = false
  ArbitraryTolerances = false
  EqualTolerance = true
  ExtensionAngle = 0
  FormatSpec = %.2f
  FormatSpecOverTolerance = %+.2f
  FormatSpecUnderTolerance = %+.2f
  Inverted = false
  LineAngle = 0
  LockPosition = false
  MeasureType = 1
  OverTolerance = 0
  References2D = -> [ProjItem006]
  Rotation = 0
  ScaleType = 0
  TheoreticalExact = false
  Type = 1
  UnderTolerance = 0
  X = -0.545356
  Y = 32.9142
FEATURE [TechDraw::DrawViewAnnotation] Annotation  label="FrontAnnotation"
  Font = Lucida Grande
  LineSpace = 80
  LockPosition = false
  MaxWidth = -1
  Rotation = 0
  ScaleType = 0
  Text = Front
  TextSize = 5
  TextStyle = 0
  X = 142
  Y = 137.5
FEATURE [TechDraw::DrawViewAnnotation] Annotation001  label="RightAnnotation"
  Font = Lucida Grande
  LineSpace = 80
  LockPosition = false
  MaxWidth = -1
  Rotation = 0
  ScaleType = 0
  Text = Right
  TextSize = 5
  TextStyle = 0
  X = 74
  Y = 137.5
FEATURE [TechDraw::DrawViewAnnotation] Annotation002  label="TopAnnotation"
  Font = Lucida Grande
  LineSpace = 80
  LockPosition = false
  MaxWidth = -1
  Rotation = 0
  ScaleType = 0
  Text = Top
  TextSize = 5
  TextStyle = 0
  X = 141
  Y = 59.5
FEATURE [TechDraw::DrawViewDimension] Dimension047
  AngleOverride = false
  Arbitrary = false
  ArbitraryTolerances = false
  EqualTolerance = true
  ExtensionAngle = 0
  FormatSpec = %.2f
  FormatSpecOverTolerance = %+.2f
  FormatSpecUnderTolerance = %+.2f
  Inverted = false
  LineAngle = 0
  LockPosition = false
  MeasureType = 1
  OverTolerance = 0
  References2D = -> [ProjItem004]
  Rotation = 0
  ScaleType = 0
  TheoreticalExact = false
  Type = 2
  UnderTolerance = 0
  X = 21.9855
  Y = 4.625
FEATURE [TechDraw::DrawPage] Page004  label="BracketDrawings"
  KeepUpdated = true
  NextBalloonIndex = 1
  ProjectionType = 0
  Template = -> Template004
  Views = -> [ProjGroup004,Dimension033,Dimension034,Dimension035,Dimension036,Dimension037,Dimension038,Dimension039,Dimension040,Dimension041,Dimension042,Dimension043,Dimension044,Dimension045,Dimension046,Annotation,Annotation001,Annotation002,Dimension047]
FEATURE [TechDraw::DrawSVGTemplate] Template005
  Height = 297
  Orientation = 0
  Width = 210
FEATURE [TechDraw::DrawSVGTemplate] Template006
  Height = 297
  Orientation = 0
  Width = 210
FEATURE [Sketcher::SketchObject] Sketch008  label="AngledSensorHoles"
  AttachmentOffset = pos=(0,0,3) rot=(0,0,1;0rad)
  ExternalGeometry = -> [Sketch005]
  FullyConstrained = true
  MapMode = 5
  Placement = pos=(0,0,3) rot=(0,0,1;0rad)
  Support = -> [XY_Plane]
  sketch-geometry (6):
    g0: LineSegment StartX=-44 StartY=-75 StartZ=0 EndX=-30 EndY=-75 EndZ=0
    g1: LineSegment StartX=30 StartY=-75 StartZ=0 EndX=44 EndY=-75 EndZ=0
    g2: Circle CenterX=-44 CenterY=-89 CenterZ=0 NormalX=0 NormalY=0 NormalZ=1 AngleXU=0 Radius=1
    g3: Circle CenterX=44 CenterY=-89 CenterZ=0 NormalX=0 NormalY=0 NormalZ=1 AngleXU=0 Radius=1
    g4: LineSegment StartX=-44 StartY=-75 StartZ=0 EndX=-44 EndY=-89 EndZ=0
    g5: LineSegment StartX=44 StartY=-75 StartZ=0 EndX=44 EndY=-89 EndZ=0
  constraints (14):
    c: Coincident(g0,g-3)
    c: Coincident(g0,g-4)
    c: Coincident(g1,g-6)
    c: Coincident(g1,g-5)
    c: Coincident(g4,g0)
    c: Coincident(g4,g2)
    c: Coincident(g5,g1)
    c: Coincident(g5,g3)
    c: Equal(g3,g-5)
    c: Equal(g2,g-3)
    c: Equal(g4,g0)
    c: Equal(g5,g1)
    c: Perpendicular(g0,g4)
    c: Perpendicular(g1,g5)
FEATURE [PartDesign::Body] Body  label="SketchMain"
  Group = -> [Sketch,Sketch001,Sketch002,Sketch003,Sketch004,Sketch005,Sketch007,Sketch008]
  Origin = -> Origin
FEATURE [PartDesign::ShapeBinder] ShapeBinder016
  Support = -> [Sketch008]
  TraceSupport = false
FEATURE [PartDesign::Pocket] Pocket011
  BaseFeature = -> Pocket010
  Direction = (0,0,-1)
  Length = 5
  Length2 = 5
  Profile = -> ShapeBinder016
  Type = 1
FEATURE [PartDesign::Body] Body001  label="ChassisPlate"
  Group = -> [ShapeBinder,Pad,ShapeBinder001,Pocket,ShapeBinder006,Pocket001,ShapeBinder007,Pocket002,ShapeBinder009,Pocket003,ShapeBinder010,Pocket004,ShapeBinder011,Pocket005,Binder003,Pocket008,Binder004,Pocket009,Binder005,Pocket010,ShapeBinder016,Pocket011]
  Origin = -> Origin001
  Tip = -> Pocket011
FEATURE [TechDraw::DrawProjGroupItem] ProjItem  label="Front"
  CoarseView = false
  Direction = (0,0,1)
  Focus = 100
  HardHidden = false
  IsoCount = 0
  IsoHidden = false
  IsoVisible = false
  LockPosition = true
  Perspective = false
  Rotation = 0
  RotationVector = (1,0,0)
  ScaleType = 2
  SeamHidden = false
  SeamVisible = true
  SmoothHidden = false
  SmoothVisible = true
  Source = -> [Body001]
  Type = 0
  X = 0
  XDirection = (-1,-1e-16,0)
  Y = 0
FEATURE [TechDraw::DrawProjGroup] ProjGroup
  Anchor = -> ProjItem
  AutoDistribute = true
  LockPosition = false
  ProjectionType = 0
  Rotation = 0
  ScaleType = 0
  Source = -> [Body001]
  Views = -> [ProjItem]
  X = 105
  Y = 148.5
  spacingX = 15
  spacingY = 15
FEATURE [TechDraw::DrawViewDimension] Dimension
  AngleOverride = false
  Arbitrary = false
  ArbitraryTolerances = false
  EqualTolerance = true
  ExtensionAngle = 0
  FormatSpec = ⌀%.2f
  FormatSpecOverTolerance = %+.2f
  FormatSpecUnderTolerance = %+.2f
  Inverted = false
  LineAngle = 0
  LockPosition = false
  MeasureType = 1
  OverTolerance = 0
  References2D = -> [ProjItem]
  Rotation = 0
  ScaleType = 0
  TheoreticalExact = false
  Type = 5
  UnderTolerance = 0
  X = 50.1529
  Y = 70.5531
FEATURE [TechDraw::DrawViewDimension] Dimension002
  AngleOverride = false
  Arbitrary = false
  ArbitraryTolerances = false
  EqualTolerance = true
  ExtensionAngle = 0
  FormatSpec = %.2f
  FormatSpecOverTolerance = %+.2f
  FormatSpecUnderTolerance = %+.2f
  Inverted = false
  LineAngle = 0
  LockPosition = false
  MeasureType = 1
  OverTolerance = 0
  References2D = -> [ProjItem]
  Rotation = 0
  ScaleType = 0
  TheoreticalExact = false
  Type = 1
  UnderTolerance = 0
  X = 2.04208
  Y = 121.051
FEATURE [TechDraw::DrawViewDimension] Dimension004
  AngleOverride = false
  Arbitrary = false
  ArbitraryTolerances = false
  EqualTolerance = true
  ExtensionAngle = 0
  FormatSpec = %.2f
  FormatSpecOverTolerance = %+.2f
  FormatSpecUnderTolerance = %+.2f
  Inverted = false
  LineAngle = 0
  LockPosition = false
  MeasureType = 1
  OverTolerance = 0
  References2D = -> [ProjItem]
  Rotation = 0
  ScaleType = 0
  TheoreticalExact = false
  Type = 1
  UnderTolerance = 0
  X = 1.29717
  Y = 110.802
FEATURE [TechDraw::DrawViewDimension] Dimension005
  AngleOverride = false
  Arbitrary = false
  ArbitraryTolerances = false
  EqualTolerance = true
  ExtensionAngle = 0
  FormatSpec = %.2f
  FormatSpecOverTolerance = %+.2f
  FormatSpecUnderTolerance = %+.2f
  Inverted = false
  LineAngle = 0
  LockPosition = false
  MeasureType = 1
  OverTolerance = 0
  References2D = -> [ProjItem]
  Rotation = 0
  ScaleType = 0
  TheoreticalExact = false
  Type = 2
  UnderTolerance = 0
  X = 83.6298
  Y = 95.1317
FEATURE [TechDraw::DrawViewDimension] Dimension006
  AngleOverride = false
  Arbitrary = false
  ArbitraryTolerances = false
  EqualTolerance = true
  ExtensionAngle = 0
  FormatSpec = %.2f
  FormatSpecOverTolerance = %+.2f
  FormatSpecUnderTolerance = %+.2f
  Inverted = false
  LineAngle = 0
  LockPosition = false
  MeasureType = 1
  OverTolerance = 0
  References2D = -> [ProjItem]
  Rotation = 0
  ScaleType = 0
  TheoreticalExact = false
  Type = 2
  UnderTolerance = 0
  X = 86.1661
  Y = 1.23328
FEATURE [TechDraw::DrawViewDimension] Dimension007
  AngleOverride = false
  Arbitrary = false
  ArbitraryTolerances = false
  EqualTolerance = true
  ExtensionAngle = 0
  FormatSpec = %.2f
  FormatSpecOverTolerance = %+.2f
  FormatSpecUnderTolerance = %+.2f
  Inverted = false
  LineAngle = 0
  LockPosition = false
  MeasureType = 1
  OverTolerance = 0
  References2D = -> [ProjItem]
  Rotation = 0
  ScaleType = 0
  TheoreticalExact = false
  Type = 2
  UnderTolerance = 0
  X = 28.9009
  Y = -87.2406
FEATURE [TechDraw::DrawViewDimension] Dimension008
  AngleOverride = false
  Arbitrary = false
  ArbitraryTolerances = false
  EqualTolerance = true
  ExtensionAngle = 0
  FormatSpec = %.2f
  FormatSpecOverTolerance = %+.2f
  FormatSpecUnderTolerance = %+.2f
  Inverted = false
  LineAngle = 0
  LockPosition = false
  MeasureType = 1
  OverTolerance = 0
  References2D = -> [ProjItem]
  Rotation = 0
  ScaleType = 0
  TheoreticalExact = false
  Type = 1
  UnderTolerance = 0
  X = 0.423435
  Y = -60.3088
FEATURE [TechDraw::DrawViewDimension] Dimension009
  AngleOverride = false
  Arbitrary = false
  ArbitraryTolerances = false
  EqualTolerance = true
  ExtensionAngle = 0
  FormatSpec = %.2f
  FormatSpecOverTolerance = %+.2f
  FormatSpecUnderTolerance = %+.2f
  Inverted = false
  LineAngle = 0
  LockPosition = false
  MeasureType = 1
  OverTolerance = 0
  References2D = -> [ProjItem]
  Rotation = 0
  ScaleType = 0
  TheoreticalExact = false
  Type = 1
  UnderTolerance = 0
  X = -69
  Y = 72.7358
FEATURE [TechDraw::DrawViewDimension] Dimension010
  AngleOverride = false
  Arbitrary = false
  ArbitraryTolerances = false
  EqualTolerance = true
  ExtensionAngle = 0
  FormatSpec = %.2f
  FormatSpecOverTolerance = %+.2f
  FormatSpecUnderTolerance = %+.2f
  Inverted = false
  LineAngle = 0
  LockPosition = false
  MeasureType = 1
  OverTolerance = 0
  References2D = -> [ProjItem]
  Rotation = 0
  ScaleType = 0
  TheoreticalExact = false
  Type = 2
  UnderTolerance = 0
  X = -52.7358
  Y = 53.9906
FEATURE [TechDraw::DrawViewDimension] Dimension011
  AngleOverride = false
  Arbitrary = false
  ArbitraryTolerances = false
  EqualTolerance = true
  ExtensionAngle = 0
  FormatSpec = %.2f
  FormatSpecOverTolerance = %+.2f
  FormatSpecUnderTolerance = %+.2f
  Inverted = false
  LineAngle = 0
  LockPosition = false
  MeasureType = 1
  OverTolerance = 0
  References2D = -> [ProjItem]
  Rotation = 0
  ScaleType = 0
  TheoreticalExact = false
  Type = 2
  UnderTolerance = 0
  X = -53.1368
  Y = 83.3939
FEATURE [TechDraw::DrawViewDimension] Dimension014
  AngleOverride = false
  Arbitrary = false
  ArbitraryTolerances = false
  EqualTolerance = true
  ExtensionAngle = 0
  FormatSpec = ⌀%.2f
  FormatSpecOverTolerance = %+.2f
  FormatSpecUnderTolerance = %+.2f
  Inverted = false
  LineAngle = 0
  LockPosition = false
  MeasureType = 1
  OverTolerance = 0
  References2D = -> [ProjItem]
  Rotation = 0
  ScaleType = 0
  TheoreticalExact = false
  Type = 5
  UnderTolerance = 0
  X = 30.6276
  Y = -55.1297
FEATURE [TechDraw::DrawViewDimension] Dimension022
  AngleOverride = false
  Arbitrary = false
  ArbitraryTolerances = false
  EqualTolerance = true
  ExtensionAngle = 0
  FormatSpec = %.2f
  FormatSpecOverTolerance = %+.2f
  FormatSpecUnderTolerance = %+.2f
  Inverted = false
  LineAngle = 0
  LockPosition = false
  MeasureType = 1
  OverTolerance = 0
  References2D = -> [ProjItem]
  Rotation = 0
  ScaleType = 0
  TheoreticalExact = false
  Type = 1
  UnderTolerance = 0
  X = -50.6554
  Y = 111.263
FEATURE [TechDraw::DrawViewDimension] Dimension023
  AngleOverride = false
  Arbitrary = false
  ArbitraryTolerances = false
  EqualTolerance = true
  ExtensionAngle = 0
  FormatSpec = %.2f
  FormatSpecOverTolerance = %+.2f
  FormatSpecUnderTolerance = %+.2f
  Inverted = false
  LineAngle = 0
  LockPosition = false
  MeasureType = 1
  OverTolerance = 0
  References2D = -> [ProjItem]
  Rotation = 0
  ScaleType = 0
  TheoreticalExact = false
  Type = 1
  UnderTolerance = 0
  X = 50
  Y = 110.28
FEATURE [TechDraw::DrawViewDimension] Dimension024
  AngleOverride = false
  Arbitrary = false
  ArbitraryTolerances = false
  EqualTolerance = true
  ExtensionAngle = 0
  FormatSpec = %.2f
  FormatSpecOverTolerance = %+.2f
  FormatSpecUnderTolerance = %+.2f
  Inverted = false
  LineAngle = 0
  LockPosition = false
  MeasureType = 1
  OverTolerance = 0
  References2D = -> [ProjItem]
  Rotation = 0
  ScaleType = 0
  TheoreticalExact = false
  Type = 1
  UnderTolerance = 0
  X = -41.0473
  Y = -60.1593
FEATURE [TechDraw::DrawPage] Page  label="CuttingDimensions"
  KeepUpdated = true
  NextBalloonIndex = 1
  ProjectionType = 0
  Template = -> Template
  Views = -> [ProjGroup,Dimension,Dimension002,Dimension004,Dimension005,Dimension006,Dimension007,Dimension008,Dimension009,Dimension010,Dimension011,Dimension014,Dimension022,Dimension023,Dimension024]
FEATURE [TechDraw::DrawProjGroupItem] ProjItem002  label="Front002"
  CoarseView = false
  Direction = (0,0,1)
  Focus = 100
  HardHidden = false
  IsoCount = 0
  IsoHidden = false
  IsoVisible = false
  LockPosition = true
  Perspective = false
  Rotation = 0
  RotationVector = (-1,0,0)
  ScaleType = 2
  SeamHidden = false
  SeamVisible = true
  SmoothHidden = false
  SmoothVisible = true
  Source = -> [Body001]
  Type = 0
  X = 0
  XDirection = (-1,0,0)
  Y = 0
FEATURE [TechDraw::DrawProjGroup] ProjGroup002
  Anchor = -> ProjItem002
  AutoDistribute = true
  LockPosition = false
  ProjectionType = 0
  Rotation = 0
  ScaleType = 0
  Source = -> [Body001]
  Views = -> [ProjItem002]
  X = 105
  Y = 148.5
  spacingX = 15
  spacingY = 15
FEATURE [TechDraw::DrawViewDimension] Dimension026
  AngleOverride = false
  Arbitrary = false
  ArbitraryTolerances = false
  EqualTolerance = true
  ExtensionAngle = 0
  FormatSpec = ⌀%.2f
  FormatSpecOverTolerance = %+.2f
  FormatSpecUnderTolerance = %+.2f
  Inverted = false
  LineAngle = 0
  LockPosition = false
  MeasureType = 1
  OverTolerance = 0
  References2D = -> [ProjItem002]
  Rotation = 0
  ScaleType = 0
  TheoreticalExact = false
  Type = 5
  UnderTolerance = 0
  X = 38.1284
  Y = 75.0527
FEATURE [TechDraw::DrawViewDimension] Dimension027
  AngleOverride = false
  Arbitrary = false
  ArbitraryTolerances = false
  EqualTolerance = true
  ExtensionAngle = 0
  FormatSpec = ⌀%.2f
  FormatSpecOverTolerance = %+.2f
  FormatSpecUnderTolerance = %+.2f
  Inverted = false
  LineAngle = 0
  LockPosition = false
  MeasureType = 1
  OverTolerance = 0
  References2D = -> [ProjItem002]
  Rotation = 0
  ScaleType = 0
  TheoreticalExact = false
  Type = 5
  UnderTolerance = 0
  X = -12.5
  Y = 69.0146
FEATURE [TechDraw::DrawViewDimension] Dimension048
  AngleOverride = false
  Arbitrary = false
  ArbitraryTolerances = false
  EqualTolerance = true
  ExtensionAngle = 0
  FormatSpec = %.2f
  FormatSpecOverTolerance = %+.2f
  FormatSpecUnderTolerance = %+.2f
  Inverted = false
  LineAngle = 0
  LockPosition = false
  MeasureType = 1
  OverTolerance = 0
  References2D = -> [ProjItem002]
  Rotation = 0
  ScaleType = 0
  TheoreticalExact = false
  Type = 2
  UnderTolerance = 0
  X = -82.4306
  Y = -95.3056
FEATURE [TechDraw::DrawViewDimension] Dimension049
  AngleOverride = false
  Arbitrary = false
  ArbitraryTolerances = false
  EqualTolerance = true
  ExtensionAngle = 0
  FormatSpec = %.2f
  FormatSpecOverTolerance = %+.2f
  FormatSpecUnderTolerance = %+.2f
  Inverted = false
  LineAngle = 0
  LockPosition = false
  MeasureType = 1
  OverTolerance = 0
  References2D = -> [ProjItem002]
  Rotation = 0
  ScaleType = 0
  TheoreticalExact = false
  Type = 1
  UnderTolerance = 0
  X = -73
  Y = -106.819
FEATURE [TechDraw::DrawViewDimension] Dimension050
  AngleOverride = false
  Arbitrary = false
  ArbitraryTolerances = false
  EqualTolerance = true
  ExtensionAngle = 0
  FormatSpec = ⌀%.2f
  FormatSpecOverTolerance = %+.2f
  FormatSpecUnderTolerance = %+.2f
  Inverted = false
  LineAngle = 0
  LockPosition = false
  MeasureType = 1
  OverTolerance = 0
  References2D = -> [ProjItem002]
  Rotation = 0
  ScaleType = 0
  TheoreticalExact = false
  Type = 5
  UnderTolerance = 0
  X = -40.625
  Y = -73.2639
FEATURE [TechDraw::DrawViewDimension] Dimension051
  AngleOverride = false
  Arbitrary = false
  ArbitraryTolerances = false
  EqualTolerance = true
  ExtensionAngle = 0
  FormatSpec = %.2f
  FormatSpecOverTolerance = %+.2f
  FormatSpecUnderTolerance = %+.2f
  Inverted = false
  LineAngle = 0
  LockPosition = false
  MeasureType = 1
  OverTolerance = 0
  References2D = -> [ProjItem002]
  Rotation = 0
  ScaleType = 0
  TheoreticalExact = false
  Type = 2
  UnderTolerance = 0
  X = -17.6667
  Y = 89.1528
FEATURE [TechDraw::DrawViewDimension] Dimension052
  AngleOverride = false
  Arbitrary = false
  ArbitraryTolerances = false
  EqualTolerance = true
  ExtensionAngle = 0
  FormatSpec = %.2f
  FormatSpecOverTolerance = %+.2f
  FormatSpecUnderTolerance = %+.2f
  Inverted = false
  LineAngle = 0
  LockPosition = false
  MeasureType = 1
  OverTolerance = 0
  References2D = -> [ProjItem002]
  Rotation = 0
  ScaleType = 0
  TheoreticalExact = false
  Type = 2
  UnderTolerance = 0
  X = -67.5
  Y = -73
FEATURE [TechDraw::DrawViewDimension] Dimension053
  AngleOverride = false
  Arbitrary = false
  ArbitraryTolerances = false
  EqualTolerance = true
  ExtensionAngle = 0
  FormatSpec = %.2f
  FormatSpecOverTolerance = %+.2f
  FormatSpecUnderTolerance = %+.2f
  Inverted = false
  LineAngle = 0
  LockPosition = false
  MeasureType = 1
  OverTolerance = 0
  References2D = -> [ProjItem002]
  Rotation = 0
  ScaleType = 0
  TheoreticalExact = false
  Type = 1
  UnderTolerance = 0
  X = -59.8472
  Y = 70.2778
FEATURE [TechDraw::DrawViewDimension] Dimension054
  AngleOverride = false
  Arbitrary = false
  ArbitraryTolerances = false
  EqualTolerance = true
  ExtensionAngle = 0
  FormatSpec = %.2f
  FormatSpecOverTolerance = %+.2f
  FormatSpecUnderTolerance = %+.2f
  Inverted = false
  LineAngle = 0
  LockPosition = false
  MeasureType = 1
  OverTolerance = 0
  References2D = -> [ProjItem002]
  Rotation = 0
  ScaleType = 0
  TheoreticalExact = false
  Type = 1
  UnderTolerance = 0
  X = -37.3472
  Y = 69.9306
FEATURE [TechDraw::DrawPage] Page002  label="ChassisBevelTemplate"
  KeepUpdated = true
  NextBalloonIndex = 1
  ProjectionType = 0
  Template = -> Template002
  Views = -> [ProjGroup002,Dimension026,Dimension027,Dimension048,Dimension049,Dimension050,Dimension051,Dimension052,Dimension053,Dimension054]
FEATURE [TechDraw::DrawProjGroupItem] ProjItem008  label="Front005"
  CoarseView = false
  Direction = (0,0,1)
  Focus = 100
  HardHidden = false
  IsoCount = 0
  IsoHidden = false
  IsoVisible = false
  LockPosition = true
  Perspective = false
  Rotation = 0
  RotationVector = (1,0,0)
  ScaleType = 2
  SeamHidden = false
  SeamVisible = true
  SmoothHidden = false
  SmoothVisible = true
  Source = -> [Body001,Body007,Body008,Body009]
  Type = 0
  X = 0
  XDirection = (1,0,0)
  Y = 0
FEATURE [TechDraw::DrawProjGroup] ProjGroup005
  Anchor = -> ProjItem008
  AutoDistribute = true
  LockPosition = false
  ProjectionType = 0
  Rotation = 0
  ScaleType = 0
  Source = -> [Body001,Body007,Body008,Body009]
  Views = -> [ProjItem008]
  X = 105
  Y = 148.5
  spacingX = 15
  spacingY = 15
FEATURE [TechDraw::DrawViewDimension] Dimension055
  AngleOverride = false
  Arbitrary = false
  ArbitraryTolerances = false
  EqualTolerance = true
  ExtensionAngle = 0
  FormatSpec = %.2f
  FormatSpecOverTolerance = %+.2f
  FormatSpecUnderTolerance = %+.2f
  Inverted = false
  LineAngle = 0
  LockPosition = false
  MeasureType = 1
  OverTolerance = 0
  References2D = -> [ProjItem008]
  Rotation = 0
  ScaleType = 0
  TheoreticalExact = false
  Type = 2
  UnderTolerance = 0
  X = -11.8456
  Y = -84.3766
FEATURE [TechDraw::DrawViewDimension] Dimension056
  AngleOverride = false
  Arbitrary = false
  ArbitraryTolerances = false
  EqualTolerance = true
  ExtensionAngle = 0
  FormatSpec = %.2f
  FormatSpecOverTolerance = %+.2f
  FormatSpecUnderTolerance = %+.2f
  Inverted = false
  LineAngle = 0
  LockPosition = false
  MeasureType = 1
  OverTolerance = 0
  References2D = -> [ProjItem008]
  Rotation = 0
  ScaleType = 0
  TheoreticalExact = false
  Type = 1
  UnderTolerance = 0
  X = -59.2753
  Y = -64.1585
FEATURE [TechDraw::DrawViewDimension] Dimension057
  AngleOverride = false
  Arbitrary = false
  ArbitraryTolerances = false
  EqualTolerance = true
  ExtensionAngle = 0
  FormatSpec = %.2f
  FormatSpecOverTolerance = %+.2f
  FormatSpecUnderTolerance = %+.2f
  Inverted = false
  LineAngle = 0
  LockPosition = false
  MeasureType = 1
  OverTolerance = 0
  References2D = -> [ProjItem008]
  Rotation = 0
  ScaleType = 0
  TheoreticalExact = false
  Type = 1
  UnderTolerance = 0
  X = -36.7753
  Y = -64.3832
FEATURE [TechDraw::DrawViewDimension] Dimension058
  AngleOverride = false
  Arbitrary = false
  ArbitraryTolerances = false
  EqualTolerance = true
  ExtensionAngle = 0
  FormatSpec = %.2f
  FormatSpecOverTolerance = %+.2f
  FormatSpecUnderTolerance = %+.2f
  Inverted = false
  LineAngle = 0
  LockPosition = false
  MeasureType = 1
  OverTolerance = 0
  References2D = -> [ProjItem008]
  Rotation = 0
  ScaleType = 0
  TheoreticalExact = false
  Type = 1
  UnderTolerance = 0
  X = -73.4493
  Y = 68.7116
FEATURE [TechDraw::DrawViewDimension] Dimension059
  AngleOverride = false
  Arbitrary = false
  ArbitraryTolerances = false
  EqualTolerance = true
  ExtensionAngle = 0
  FormatSpec = %.2f
  FormatSpecOverTolerance = %+.2f
  FormatSpecUnderTolerance = %+.2f
  Inverted = false
  LineAngle = 0
  LockPosition = false
  MeasureType = 1
  OverTolerance = 0
  References2D = -> [ProjItem008]
  Rotation = 0
  ScaleType = 0
  TheoreticalExact = false
  Type = 2
  UnderTolerance = 0
  X = -67.5
  Y = 77
FEATURE [TechDraw::DrawViewDimension] Dimension060
  AngleOverride = false
  Arbitrary = false
  ArbitraryTolerances = false
  EqualTolerance = true
  ExtensionAngle = 0
  FormatSpec = %.2f
  FormatSpecOverTolerance = %+.2f
  FormatSpecUnderTolerance = %+.2f
  Inverted = false
  LineAngle = 0
  LockPosition = false
  MeasureType = 1
  OverTolerance = 0
  References2D = -> [ProjItem008]
  Rotation = 0
  ScaleType = 0
  TheoreticalExact = false
  Type = 2
  UnderTolerance = 0
  X = -60.4902
  Y = 87.8676
FEATURE [TechDraw::DrawViewDimension] Dimension061
  AngleOverride = false
  Arbitrary = false
  ArbitraryTolerances = false
  EqualTolerance = true
  ExtensionAngle = 0
  FormatSpec = ⌀%.2f
  FormatSpecOverTolerance = %+.2f
  FormatSpecUnderTolerance = %+.2f
  Inverted = false
  LineAngle = 0
  LockPosition = false
  MeasureType = 1
  OverTolerance = 0
  References2D = -> [ProjItem008]
  Rotation = 0
  ScaleType = 0
  TheoreticalExact = false
  Type = 5
  UnderTolerance = 0
  X = 51.4502
  Y = 90.094
FEATURE [TechDraw::DrawViewDimension] Dimension062
  AngleOverride = false
  Arbitrary = false
  ArbitraryTolerances = false
  EqualTolerance = true
  ExtensionAngle = 0
  FormatSpec = ⌀%.2f
  FormatSpecOverTolerance = %+.2f
  FormatSpecUnderTolerance = %+.2f
  Inverted = false
  LineAngle = 0
  LockPosition = false
  MeasureType = 1
  OverTolerance = 0
  References2D = -> [ProjItem008]
  Rotation = 0
  ScaleType = 0
  TheoreticalExact = false
  Type = 5
  UnderTolerance = 0
  X = -13.9297
  Y = -64.9306
FEATURE [TechDraw::DrawPage] Page005
  KeepUpdated = true
  NextBalloonIndex = 1
  ProjectionType = 0
  Template = -> Template005
  Views = -> [ProjGroup005,Dimension055,Dimension056,Dimension057,Dimension058,Dimension059,Dimension060,Dimension061,Dimension062]
FEATURE [TechDraw::DrawProjGroupItem] ProjItem009  label="Front006"
  CoarseView = false
  Direction = (0,0,1)
  Focus = 100
  HardHidden = false
  IsoCount = 0
  IsoHidden = false
  IsoVisible = false
  LockPosition = true
  Perspective = false
  Rotation = 0
  RotationVector = (1,0,0)
  ScaleType = 2
  SeamHidden = false
  SeamVisible = true
  SmoothHidden = false
  SmoothVisible = true
  Source = -> [Body001]
  Type = 0
  X = 0
  XDirection = (1,0,0)
  Y = 0
FEATURE [TechDraw::DrawProjGroup] ProjGroup006
  Anchor = -> ProjItem009
  AutoDistribute = true
  LockPosition = false
  ProjectionType = 0
  Rotation = 0
  ScaleType = 0
  Source = -> [Body001]
  Views = -> [ProjItem009]
  X = 105
  Y = 148.5
  spacingX = 15
  spacingY = 15
FEATURE [TechDraw::DrawViewDimension] Dimension066
  AngleOverride = false
  Arbitrary = false
  ArbitraryTolerances = false
  EqualTolerance = true
  ExtensionAngle = 0
  FormatSpec = %.2f
  FormatSpecOverTolerance = %+.2f
  FormatSpecUnderTolerance = %+.2f
  Inverted = false
  LineAngle = 0
  LockPosition = false
  MeasureType = 1
  OverTolerance = 0
  References2D = -> [ProjItem009]
  Rotation = 0
  ScaleType = 0
  TheoreticalExact = false
  Type = 2
  UnderTolerance = 0
  X = -83.2519
  Y = -29.7281
FEATURE [TechDraw::DrawViewDimension] Dimension067
  AngleOverride = false
  Arbitrary = false
  ArbitraryTolerances = false
  EqualTolerance = true
  ExtensionAngle = 0
  FormatSpec = ⌀%.2f
  FormatSpecOverTolerance = %+.2f
  FormatSpecUnderTolerance = %+.2f
  Inverted = false
  LineAngle = 0
  LockPosition = false
  MeasureType = 1
  OverTolerance = 0
  References2D = -> [ProjItem009]
  Rotation = 0
  ScaleType = 0
  TheoreticalExact = false
  Type = 5
  UnderTolerance = 0
  X = -28.5152
  Y = -82.3052
FEATURE [TechDraw::DrawViewDimension] Dimension068
  AngleOverride = false
  Arbitrary = false
  ArbitraryTolerances = false
  EqualTolerance = true
  ExtensionAngle = 0
  FormatSpec = ⌀%.2f
  FormatSpecOverTolerance = %+.2f
  FormatSpecUnderTolerance = %+.2f
  Inverted = false
  LineAngle = 0
  LockPosition = false
  MeasureType = 1
  OverTolerance = 0
  References2D = -> [ProjItem009]
  Rotation = 0
  ScaleType = 0
  TheoreticalExact = false
  Type = 5
  UnderTolerance = 0
  X = -45.6081
  Y = -17.1739
FEATURE [TechDraw::DrawViewDimension] Dimension069
  AngleOverride = false
  Arbitrary = false
  ArbitraryTolerances = false
  EqualTolerance = true
  ExtensionAngle = 0
  FormatSpec = %.2f
  FormatSpecOverTolerance = %+.2f
  FormatSpecUnderTolerance = %+.2f
  Inverted = false
  LineAngle = 0
  LockPosition = false
  MeasureType = 1
  OverTolerance = 0
  References2D = -> [ProjItem009]
  Rotation = 0
  ScaleType = 0
  TheoreticalExact = false
  Type = 2
  UnderTolerance = 0
  X = -57.9309
  Y = -80.243
FEATURE [TechDraw::DrawPage] Page006
  KeepUpdated = true
  NextBalloonIndex = 1
  ProjectionType = 0
  Template = -> Template006
  Views = -> [ProjGroup006,Dimension066,Dimension067,Dimension068,Dimension069]
